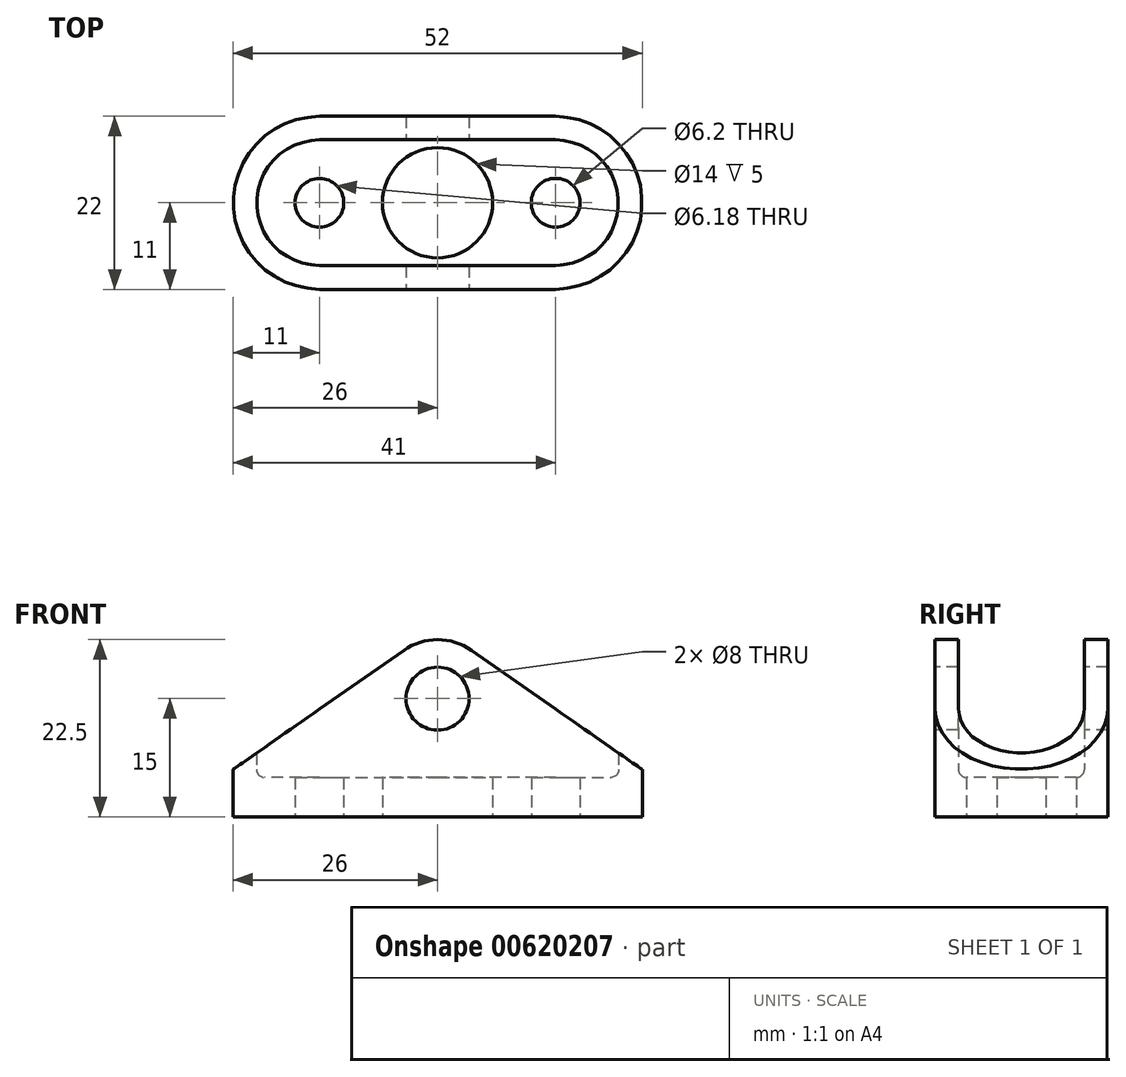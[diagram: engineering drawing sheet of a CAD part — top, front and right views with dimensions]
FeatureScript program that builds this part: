
annotation { "Feature Type Name" : "Feature", "Feature Type Description" : "" }
export const myFeature = defineFeature(function(context is Context, id is Id, definition is map)
    precondition{}
    {
        {
            var Q0;
            Q0=qCreatedBy(makeId("Top.planeOp"),FACE);
            var sketch = newSketch(context, id + "F0", { "sketchPlane" : qUnion([Q0])});
            skLineSegment(sketch, "E0", {"start": v(-15, 0) * mm, "end": v(15, 0) * mm});
            skArc(sketch, "E1.0.startCap", {"start": v(-15, -11) * mm, "mid": v(-26, 0) * mm, "end": v(-15, 11) * mm});
            skArc(sketch, "E1.0.endCap", {"start": v(15, 11) * mm, "mid": v(26, 0) * mm, "end": v(15, -11) * mm});
            skLineSegment(sketch, "E1.0.left", {"start": v(-15, 11) * mm, "end": v(15, 11) * mm});
            skLineSegment(sketch, "E1.0.right", {"start": v(-15, -11) * mm, "end": v(15, -11) * mm});
            skCircle(sketch, "E2", {"center": v(-15, 0) * mm, "radius": 3.09 * mm});
            skCircle(sketch, "E3", {"center": v(15, 0) * mm, "radius": 3.1 * mm});
            skCircle(sketch, "E4", {"center": v(0, 0) * mm, "radius": 7 * mm});
            skSolve(sketch);
        }
        {
            var Q0;
            Q0 = qSketchRegion(id + "F0", true);
            extrude(context, id + "F1", {"entities" : qUnion([Q0]), "depth" : 25 * mm, "offsetDistance" : 25 * mm});
        }
        {
            var Q0;
            Q0=makeQuery(id+"F1.opExtrude","SWEPT_FACE",FACE,{"disambiguationData":[OSD([sQuery(id+"F0.wireOp",EDGE,"E1.0.right")])]});
            var sketch = newSketch(context, id + "F2", { "sketchPlane" : qUnion([Q0])});
            skLineSegment(sketch, "E5", {"start": v(0, 0) * mm, "end": v(0, 15) * mm, "construction": true});
            skPoint(sketch, "E5.endSnap0", {"position": v(0, 25) * mm});
            skCircle(sketch, "E6", {"center": v(0, 15) * mm, "radius": 7.5 * mm, "construction": true});
            skLineSegment(sketch, "E7", {"start": v(-26, 25) * mm, "end": v(-26, 6) * mm});
            skLineSegment(sketch, "E8", {"start": v(-26, 6) * mm, "end": v(-4.3, 21.15) * mm});
            skLineSegment(sketch, "E9", {"start": v(-26, 25) * mm, "end": v(26, 25) * mm});
            skLineSegment(sketch, "E10", {"start": v(26, 25) * mm, "end": v(26, 6) * mm});
            skLineSegment(sketch, "E11", {"start": v(26, 6) * mm, "end": v(4.3, 21.15) * mm});
            skArc(sketch, "E12", {"start": v(4.3, 21.15) * mm, "mid": v(0, 22.5) * mm, "end": v(-4.3, 21.15) * mm});
            skCircle(sketch, "E13", {"center": v(0, 15) * mm, "radius": 4 * mm});
            skSolve(sketch);
        }
        {
            var Q0;
            {var subQ0=sQuery(id+"F2.wireOp",EDGE,"E12");Q0=makeQuery(id+"F2.imprint","IMPRINT",FACE,{"disambiguationData":[TD([[makeQuery(id+"F2.imprint","IMPRINT",EDGE,{"derivedFrom":subQ0}),-1.0]])]});}
            var Q1;
            Q1 = qSketchRegion(id + "F2", true);
            extrude(context, id + "F3", {"entities" : qUnion([Q0, Q1]), "operationType" : NewBodyOperationType.REMOVE, "oppositeDirection" : true, "depth" : 25 * mm, "offsetDistance" : 25 * mm});
        }
        {
            var Q0;
            Q0=makeQuery(id+"F1.opExtrude","CAP_FACE",FACE,{"disambiguationData":[OSD([sQuery(id+"F0.wireOp",EDGE,"E1.0.startCap"),sQuery(id+"F0.wireOp",EDGE,"E1.0.endCap"),sQuery(id+"F0.wireOp",EDGE,"E1.0.left"),sQuery(id+"F0.wireOp",EDGE,"E1.0.right"),sQuery(id+"F0.wireOp",EDGE,"E2"),sQuery(id+"F0.wireOp",EDGE,"E3")])],"isStart":true});
            cPlane(context, id + "F4", {"entities" : qUnion([Q0]), "cplaneType" : CPlaneType.OFFSET, "offset" : 5 * mm, "oppositeDirection" : true, "width" : 150 * mm, "height" : 150 * mm});
        }
        {
            var Q0;
            Q0=qCreatedBy(id+"F4.planeOp",FACE);
            var sketch = newSketch(context, id + "F5", { "sketchPlane" : qUnion([Q0])});
            skArc(sketch, "E14.0", {"start": v(15, -8) * mm, "mid": v(23, 0) * mm, "end": v(15, 8) * mm});
            skLineSegment(sketch, "E14.1", {"start": v(-15, -8) * mm, "end": v(15, -8) * mm});
            skArc(sketch, "E14.2", {"start": v(-15, 8) * mm, "mid": v(-23, 0) * mm, "end": v(-15, -8) * mm});
            skLineSegment(sketch, "E14.3", {"start": v(15, 8) * mm, "end": v(-15, 8) * mm});
            skSolve(sketch);
        }
        {
            var Q0;
            Q0 = qSketchRegion(id + "F5", true);
            extrude(context, id + "F6", {"entities" : qUnion([Q0]), "operationType" : NewBodyOperationType.REMOVE, "oppositeDirection" : true, "depth" : 25 * mm, "offsetDistance" : 25 * mm});
        }
        {
            var Q0;
            Q0=makeQuery(id+"F6.boolean.opBoolean","COPY",EDGE,{"derivedFrom":makeQuery(id+"F6.opExtrude","CAP_EDGE",EDGE,{"disambiguationData":[OSD([sQuery(id+"F5.wireOp",EDGE,"E14.3")])],"isStart":true})});
            fillet(context, id + "F7", {"entities" : qUnion([Q0]), "radius" : 1 * mm, "tangentPropagation" : true, "allowEdgeOverflow" : false});
        }
    });
